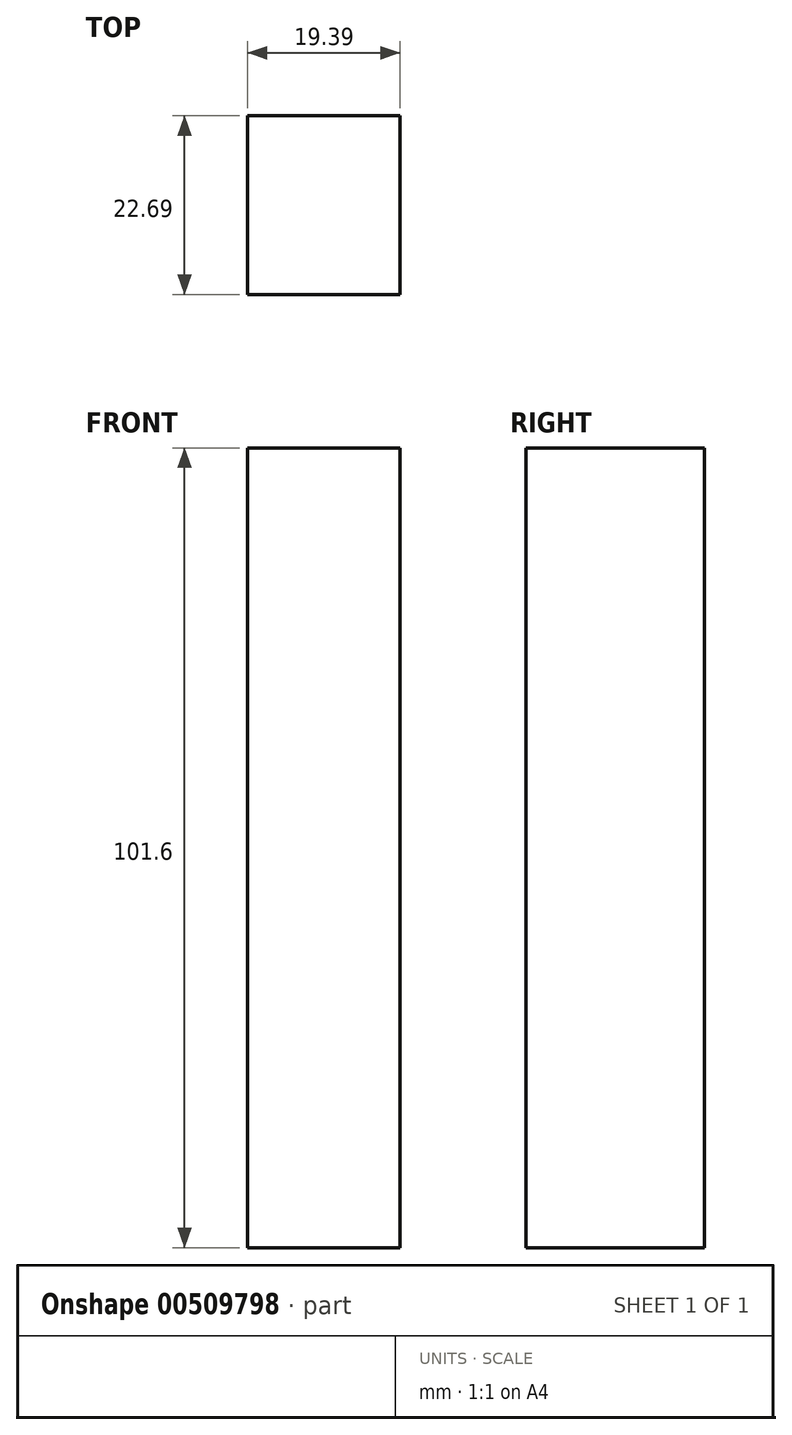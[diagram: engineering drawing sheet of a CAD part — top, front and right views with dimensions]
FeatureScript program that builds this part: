
annotation { "Feature Type Name" : "Feature", "Feature Type Description" : "" }
export const myFeature = defineFeature(function(context is Context, id is Id, definition is map)
    precondition{}
    {
        {
            var Q0;
            Q0=qCreatedBy(makeId("Top.planeOp"),FACE);
            var sketch = newSketch(context, id + "F0", { "sketchPlane" : qUnion([Q0])});
            skLineSegment(sketch, "E0.bottom", {"start": v(60.8, -61) * mm, "end": v(41.42, -61) * mm});
            skLineSegment(sketch, "E0.top", {"start": v(60.8, -38.31) * mm, "end": v(41.42, -38.31) * mm});
            skLineSegment(sketch, "E0.left", {"start": v(60.8, -61) * mm, "end": v(60.8, -38.31) * mm});
            skLineSegment(sketch, "E0.right", {"start": v(41.42, -61) * mm, "end": v(41.42, -38.31) * mm});
            skLineSegment(sketch, "E1.MirrorCS", {"start": v(60.8, -15.63) * mm, "end": v(41.42, -15.63) * mm});
            skLineSegment(sketch, "E2.MirrorCS", {"start": v(41.42, -15.63) * mm, "end": v(41.42, -38.31) * mm});
            skLineSegment(sketch, "E3.MirrorCS", {"start": v(60.8, -15.63) * mm, "end": v(60.8, -38.31) * mm});
            skSolve(sketch);
        }
        {
            var Q0;
            Q0=makeQuery(id+"F0.imprint","IMPRINT",FACE,{"disambiguationData":[TD([[makeQuery(id+"F0.imprint","IMPRINT",EDGE,{"derivedFrom":sQuery(id+"F0.wireOp",EDGE,"E0.bottom")}),-1.0]])]});
            extrude(context, id + "F1", {"entities" : qUnion([Q0]), "depth" : -101.6 * mm});
        }
    });
